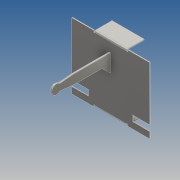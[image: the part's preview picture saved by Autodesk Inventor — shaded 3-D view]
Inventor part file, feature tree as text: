
AUTODESK INVENTOR PART (.ipt)
format: ipt  version: 2016 (Build 200138000, 138)  size: 214,016 bytes
history: native  units: mm
features: sketch x8, sheet_metal_op x7, extrude x4, other x4, fillet x1
ambient origin geometry x8: Origin, YZ Plane, XZ Plane, XY Plane, X Axis, Y Axis, Z Axis, Center Point
bodies: Solid1 (feature_tree)
feature tree (24):
  sheet_metal_op  "Face1"
  sheet_metal_op  "Flange1"
  sheet_metal_op  "Flange2"
  extrude  "Extrusion1"  Depth=45.0mm
  extrude  "Extrusion2"  Depth=0.5mm
  fillet  "Fillet1"  Radius=0.25mm
  extrude  "Extrusion3"  Depth=0.5mm
  extrude  "Extrusion4"  Depth=12.0mm TaperAngle=90.0deg
  sketch  "Sketch1"  dims[d0=53.0mm d1=45.0mm]
  other  "Plate1"
  sketch  "Sketch2"  dims[d2=0.5mm d3=0.5mm d4=0.25mm]
  other  "Plate2"
  sheet_metal_op  "Bend1"
  sheet_metal_op  "Corner1"
  sketch  "Sketch3"  dims[d5=1.0mm d6=0.5mm]
  other  "Plate3"
  sheet_metal_op  "Bend2"
  sheet_metal_op  "Corner2"
  sketch  "Sketch4"  dims[d7=22.0mm d8=12.0mm d9=90.0deg d10=0.5mm]
  sketch  "Sketch5"  dims[d11=2.0mm]
  sketch  "Sketch6"  dims[d12=0.5mm]
  sketch  "Sketch7"  dims[d13=0.5mm]
  sketch  "Sketch8"  dims[d14=0.5mm d15=0.25mm d16=1.0mm d17=0.5mm d18=22.0mm d19=12.0mm d20=90.0deg d21=0.5mm d22=2.0mm d23=0.5mm d24=0.5mm d25=4.3mm d26=4.3mm d27=30.0mm d29=4.0mm d30=0.5mm d31=0.0mm d32=5.0mm d33=0.0mm d34=3.0mm d35=5.0mm d36=0.0mm d37=5.0mm d38=6.0mm d39=3.0mm d40=10.0mm d41=3.0mm d43=8.0mm d44=1.0mm d45=3.0mm d46=1.0mm d47=12.0mm d48=3.0mm d49=40.0mm d50=0.0mm d51=6.3mm d52=4.5mm d53=10.0mm d54=6.35mm d55=6.0mm d56=40.0mm d57=0.0mm]
  other  "Cut1"
